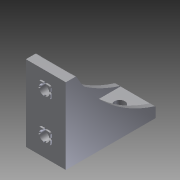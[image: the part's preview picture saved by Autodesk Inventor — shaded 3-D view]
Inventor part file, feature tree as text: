
AUTODESK INVENTOR PART (.ipt)
format: ipt  version: 2013 (Build 170138000, 138)  size: 241,664 bytes
history: native  units: mm
features: other x70, extrude x9, sketch x9, pattern_linear x2
ambient origin geometry x8: Origin, YZ Plane, XZ Plane, XY Plane, X Axis, Y Axis, Z Axis, Center Point
bodies: Solid1 (feature_tree)
feature tree (90):
  extrude  "Extrusion1"  Depth=15.0mm TaperAngle=0.0deg
  extrude  "Extrusion2"  Depth=5.0mm TaperAngle=0.0deg
  extrude  "Extrusion3"  Depth=5.0mm TaperAngle=0.0deg
  extrude  "Extrusion4"  Depth=0.8mm TaperAngle=0.0deg
  pattern_linear  "Rectangular Pattern1"  [2 undecoded]
  extrude  "Extrusion5"  [1 undecoded]
  pattern_linear  "Rectangular Pattern2"  [2 undecoded]
  extrude  "Extrusion6"  [1 undecoded]
  extrude  "Extrusion7"  [1 undecoded]
  extrude  "Extrusion8"  [1 undecoded]
  extrude  "Extrusion9"  [1 undecoded]
  other  "to_bolt_row_8_to_9_1_XY"
  other  "to_bolt_row_8_to_9_1_YZ"
  other  "to_bolt_row_8_to_9_1_ZX"
  other  "to_bolt_row_8_to_9_1_X"
  other  "to_bolt_row_8_to_9_1_Y"
  other  "to_bolt_row_8_to_9_1_Z"
  other  "to_bolt_row_8_to_9_1_Center"
  other  "to_bolt_row_8_to_9_2_XY"
  other  "to_bolt_row_8_to_9_2_YZ"
  other  "to_bolt_row_8_to_9_2_ZX"
  other  "to_bolt_row_8_to_9_2_X"
  other  "to_bolt_row_8_to_9_2_Y"
  other  "to_bolt_row_8_to_9_2_Z"
  other  "to_bolt_row_8_to_9_2_Center"
  other  "to_bolt_row_8_9_base_2_XY"
  other  "to_bolt_row_8_9_base_2_YZ"
  other  "to_bolt_row_8_9_base_2_ZX"
  other  "to_bolt_row_8_9_base_2_X"
  other  "to_bolt_row_8_9_base_2_Y"
  other  "to_bolt_row_8_9_base_2_Z"
  other  "to_bolt_row_8_9_base_2_Center"
  other  "to_bolt_row_8_9_base_1_XY"
  other  "to_bolt_row_8_9_base_1_YZ"
  other  "to_bolt_row_8_9_base_1_ZX"
  other  "to_bolt_row_8_9_base_1_X"
  other  "to_bolt_row_8_9_base_1_Y"
  other  "to_bolt_row_8_9_base_1_Z"
  other  "to_bolt_row_8_9_base_1_Center"
  other  "to_nut_row_8_to_9_2_XY"
  other  "to_nut_row_8_to_9_2_YZ"
  other  "to_nut_row_8_to_9_2_ZX"
  other  "to_nut_row_8_to_9_2_X"
  other  "to_nut_row_8_to_9_2_Y"
  other  "to_nut_row_8_to_9_2_Z"
  other  "to_nut_row_8_to_9_2_Center"
  other  "to_nut_row_8_to_9_1_XY"
  other  "to_nut_row_8_to_9_1_YZ"
  other  "to_nut_row_8_to_9_1_ZX"
  other  "to_nut_row_8_to_9_1_X"
  other  "to_nut_row_8_to_9_1_Y"
  other  "to_nut_row_8_to_9_1_Z"
  other  "to_nut_row_8_to_9_1_Center"
  other  "to_nut_row_8_9_base_2_XY"
  other  "to_nut_row_8_9_base_2_YZ"
  other  "to_nut_row_8_9_base_2_ZX"
  other  "to_nut_row_8_9_base_2_X"
  other  "to_nut_row_8_9_base_2_Y"
  other  "to_nut_row_8_9_base_2_Z"
  other  "to_nut_row_8_9_base_2_Center"
  other  "to_nut_row_8_9_base_1_XY"
  other  "to_nut_row_8_9_base_1_YZ"
  other  "to_nut_row_8_9_base_1_ZX"
  other  "to_nut_row_8_9_base_1_X"
  other  "to_nut_row_8_9_base_1_Y"
  other  "to_nut_row_8_9_base_1_Z"
  other  "to_nut_row_8_9_base_1_Center"
  other  "bracket_to_dummy_XY"
  other  "bracket_to_dummy_YZ"
  other  "bracket_to_dummy_ZX"
  other  "bracket_to_dummy_X"
  other  "bracket_to_dummy_Y"
  other  "bracket_to_dummy_Z"
  other  "bracket_to_dummy_Center"
  other  "bracket_to_bolt_XY"
  other  "bracket_to_bolt_YZ"
  other  "bracket_to_bolt_ZX"
  other  "bracket_to_bolt_X"
  other  "bracket_to_bolt_Y"
  other  "bracket_to_bolt_Z"
  other  "bracket_to_bolt_Center"
  sketch  "Sketch_15"  dims[d26=0.8mm d27=0.0mm]
  sketch  "Sketch_16"  dims[d28=1.25mm d29=0.0mm]
  sketch  "Sketch_28"
  sketch  "Sketch_6"  dims[d4=20.0mm d5=0.0mm d6=5.0mm d7=0.0mm]
  sketch  "Sketch_8"  dims[d8=20.0mm d10=20.0mm d11=10.0mm d13=0.0mm d14=5.0mm d15=0.0mm]
  sketch  "Sketch_1"  dims[d0=20.0mm d1=0.0mm d2=15.0mm d3=0.0mm]
  sketch  "Sketch_10"  dims[d16=20.0mm d18=15.0mm d19=10.0mm d21=0.0mm d22=0.8mm d23=0.0mm]
  sketch  "Sketch_13"  dims[d24=0.8mm d25=0.0mm]
  sketch  "Sketch_26"
note: 9 required parameter values undecoded (feature->parameter linkage not recoverable at this tier; creation-order binding heuristic only, values carry confidence <= 0.55)
